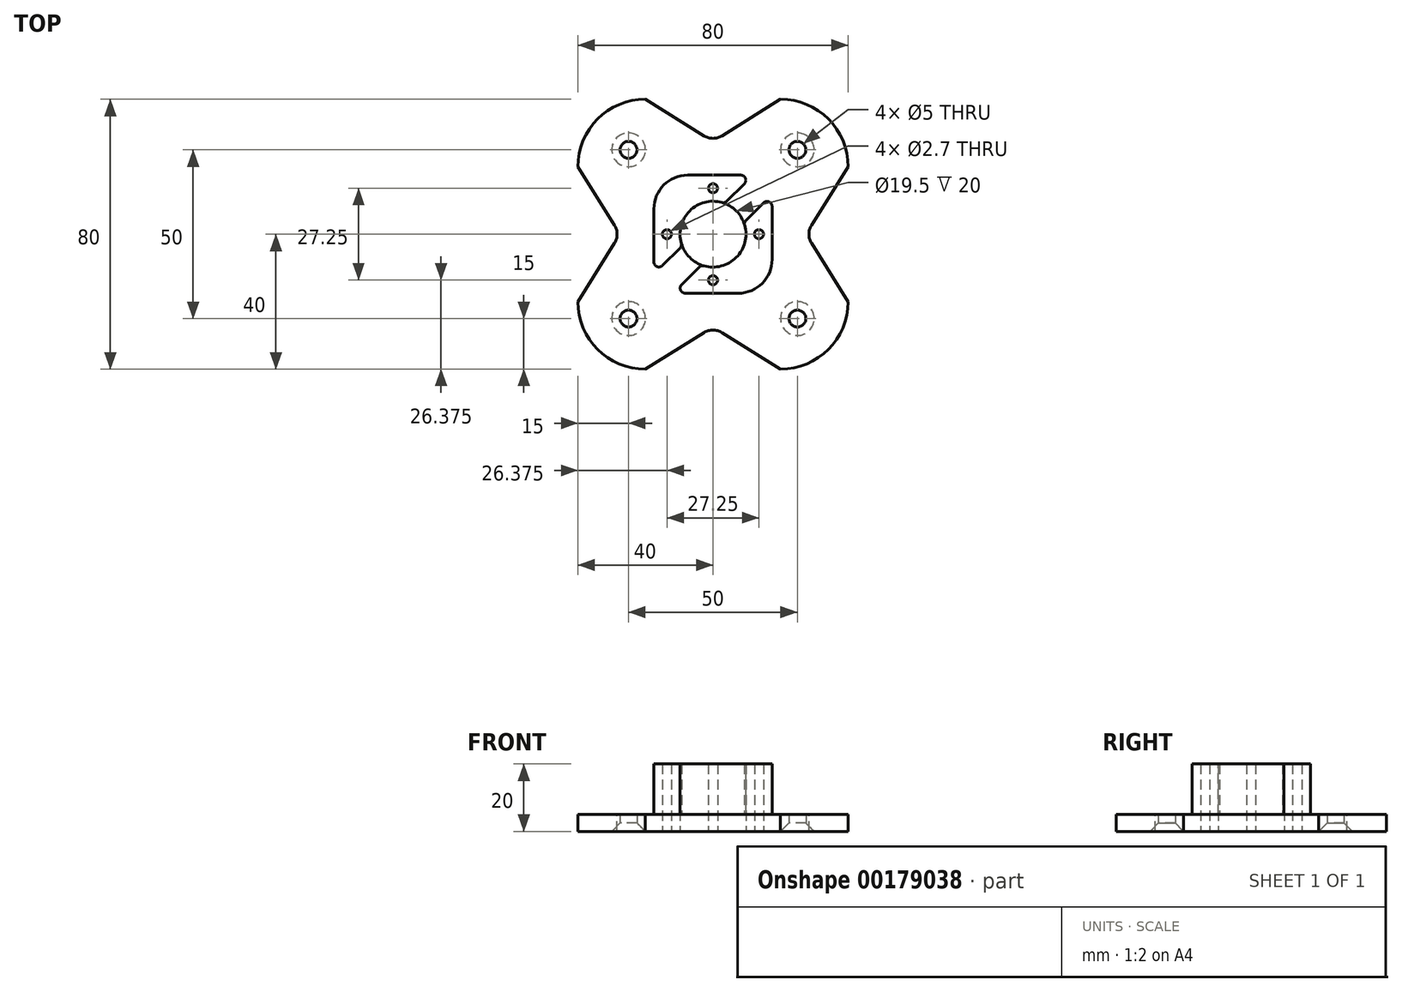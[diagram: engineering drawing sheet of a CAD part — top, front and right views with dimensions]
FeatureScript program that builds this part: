
annotation { "Feature Type Name" : "Feature", "Feature Type Description" : "" }
export const myFeature = defineFeature(function(context is Context, id is Id, definition is map)
    precondition{}
    {
        {
            var Q0;
            Q0=qCreatedBy(makeId("Top.planeOp"),FACE);
            var sketch = newSketch(context, id + "F0", { "sketchPlane" : qUnion([Q0])});
            skCircle(sketch, "E0", {"center": v(0, 0) * mm, "radius": 9.75 * mm});
            skLineSegment(sketch, "E1.bottom", {"start": v(-40, 40) * mm, "end": v(40, 40) * mm});
            skLineSegment(sketch, "E1.top", {"start": v(-40, -40) * mm, "end": v(40, -40) * mm});
            skLineSegment(sketch, "E1.left", {"start": v(-40, 40) * mm, "end": v(-40, -40) * mm});
            skLineSegment(sketch, "E1.right", {"start": v(40, 40) * mm, "end": v(40, -40) * mm});
            skCircle(sketch, "E2", {"center": v(-25, 25) * mm, "radius": 2.5 * mm});
            skCircle(sketch, "E3.0.1.0", {"center": v(-25, -25) * mm, "radius": 2.5 * mm});
            skCircle(sketch, "E3.1.0.0", {"center": v(25, 25) * mm, "radius": 2.5 * mm});
            skCircle(sketch, "E3.1.1.0", {"center": v(25, -25) * mm, "radius": 2.5 * mm});
            skLineSegment(sketch, "E3.direction1", {"start": v(-25, 25) * mm, "end": v(25, 25) * mm, "construction": true});
            skLineSegment(sketch, "E3.direction2", {"start": v(-25, 25) * mm, "end": v(-25, -25) * mm, "construction": true});
            skSolve(sketch);
        }
        {
            var Q0;
            Q0 = qSketchRegion(id + "F0", true);
            extrude(context, id + "F1", {"entities" : qUnion([Q0]), "depth" : 5 * mm});
        }
        {
            var Q0;
            Q0=makeQuery(id+"F1.opExtrude","CAP_EDGE",EDGE,{"disambiguationData":[OSD([sQuery(id+"F0.wireOp",EDGE,"E3.1.0.0")])],"isStart":true});
            var Q1;
            Q1=makeQuery(id+"F1.opExtrude","CAP_EDGE",EDGE,{"disambiguationData":[OSD([sQuery(id+"F0.wireOp",EDGE,"E2")])],"isStart":true});
            var Q2;
            Q2=makeQuery(id+"F1.opExtrude","CAP_EDGE",EDGE,{"disambiguationData":[OSD([sQuery(id+"F0.wireOp",EDGE,"E3.0.1.0")])],"isStart":true});
            var Q3;
            Q3=makeQuery(id+"F1.opExtrude","CAP_EDGE",EDGE,{"disambiguationData":[OSD([sQuery(id+"F0.wireOp",EDGE,"E3.1.1.0")])],"isStart":true});
            chamfer(context, id + "F2", {"entities" : qUnion([Q0, Q1, Q2, Q3]), "width" : 2.5 * mm, "tangentPropagation" : true});
        }
        {
            var Q0;
            Q0=makeQuery(id+"F1.opExtrude","CAP_FACE",FACE,{"disambiguationData":[OSD([sQuery(id+"F0.wireOp",EDGE,"E0"),sQuery(id+"F0.wireOp",EDGE,"E1.bottom"),sQuery(id+"F0.wireOp",EDGE,"E1.top"),sQuery(id+"F0.wireOp",EDGE,"E1.left"),sQuery(id+"F0.wireOp",EDGE,"E1.right"),sQuery(id+"F0.wireOp",EDGE,"E2"),sQuery(id+"F0.wireOp",EDGE,"E3.0.1.0"),sQuery(id+"F0.wireOp",EDGE,"E3.1.0.0"),sQuery(id+"F0.wireOp",EDGE,"E3.1.1.0")])],"isStart":false});
            var sketch = newSketch(context, id + "F3", { "sketchPlane" : qUnion([Q0])});
            skArc(sketch, "E4.0", {"start": v(-3.46, -9.12) * mm, "mid": v(6.9, -6.9) * mm, "end": v(9.12, 3.46) * mm});
            skLineSegment(sketch, "E5", {"start": v(-13.05, -7.4) * mm, "end": v(-9.12, -3.46) * mm});
            skLineSegment(sketch, "E6", {"start": v(-7.4, -13.05) * mm, "end": v(-3.46, -9.12) * mm});
            skArc(sketch, "E7.trimOffspring", {"start": v(3.46, 9.12) * mm, "mid": v(-6.9, 6.9) * mm, "end": v(-9.12, -3.46) * mm});
            skLineSegment(sketch, "E8.trimOffspring", {"start": v(3.46, 9.12) * mm, "end": v(7.4, 13.05) * mm});
            skLineSegment(sketch, "E9.trimOffspring", {"start": v(9.12, 3.46) * mm, "end": v(13.05, 7.4) * mm});
            skLineSegment(sketch, "E10", {"start": v(0, 0) * mm, "end": v(17.61, 17.61) * mm, "construction": true});
            skLineSegment(sketch, "E11.bottom", {"start": v(-17.5, 17.5) * mm, "end": v(17.5, 17.5) * mm});
            skLineSegment(sketch, "E11.top", {"start": v(-17.5, -17.5) * mm, "end": v(17.5, -17.5) * mm});
            skLineSegment(sketch, "E11.left", {"start": v(-17.5, 17.5) * mm, "end": v(-17.5, -17.5) * mm});
            skLineSegment(sketch, "E11.right", {"start": v(17.5, 17.5) * mm, "end": v(17.5, -17.5) * mm});
            skLineSegment(sketch, "E12", {"start": v(7.4, 13.05) * mm, "end": v(11.84, 17.5) * mm});
            skLineSegment(sketch, "E13", {"start": v(13.05, 7.4) * mm, "end": v(17.5, 11.84) * mm});
            skLineSegment(sketch, "E14", {"start": v(-13.05, -7.4) * mm, "end": v(-17.5, -11.84) * mm});
            skLineSegment(sketch, "E15", {"start": v(-7.4, -13.05) * mm, "end": v(-11.84, -17.5) * mm});
            skCircle(sketch, "E16", {"center": v(0, 13.63) * mm, "radius": 1.35 * mm});
            skCircle(sketch, "E17.1.0", {"center": v(-13.63, 0) * mm, "radius": 1.35 * mm});
            skCircle(sketch, "E17.2.0", {"center": v(0, -13.63) * mm, "radius": 1.35 * mm});
            skCircle(sketch, "E17.3.0", {"center": v(13.63, 0) * mm, "radius": 1.35 * mm});
            skLineSegment(sketch, "E18", {"start": v(0, 9.75) * mm, "end": v(0, 17.5) * mm, "construction": true});
            skSolve(sketch);
        }
        {
            var Q0;
            Q0=makeQuery(id+"F3.imprint","IMPRINT",FACE,{"disambiguationData":[TD([[makeQuery(id+"F3.imprint","IMPRINT",EDGE,{"derivedFrom":sQuery(id+"F3.wireOp",EDGE,"E4.0")}),-1.0]])]});
            var Q1;
            Q1=makeQuery(id+"F3.imprint","IMPRINT",FACE,{"disambiguationData":[TD([[makeQuery(id+"F3.imprint","IMPRINT",EDGE,{"derivedFrom":sQuery(id+"F3.wireOp",EDGE,"E5")}),1.0]])]});
            extrude(context, id + "F4", {"entities" : qUnion([Q0, Q1]), "operationType" : NewBodyOperationType.ADD, "depth" : 15 * mm});
        }
        {
            var Q0;
            Q0=makeQuery(id+"F4.boolean.opBoolean","SPLIT",FACE,{"disambiguationData":[TD([makeQuery(id+"F4.opExtrude","SWEPT_FACE",FACE,{"disambiguationData":[OSD([sQuery(id+"F3.wireOp",EDGE,"E17.1.0")])]})])],"derivedFrom":makeQuery(id+"F1.opExtrude","CAP_FACE",FACE,{"disambiguationData":[OSD([sQuery(id+"F0.wireOp",EDGE,"E0"),sQuery(id+"F0.wireOp",EDGE,"E1.bottom"),sQuery(id+"F0.wireOp",EDGE,"E1.top"),sQuery(id+"F0.wireOp",EDGE,"E1.left"),sQuery(id+"F0.wireOp",EDGE,"E1.right"),sQuery(id+"F0.wireOp",EDGE,"E2"),sQuery(id+"F0.wireOp",EDGE,"E3.0.1.0"),sQuery(id+"F0.wireOp",EDGE,"E3.1.0.0"),sQuery(id+"F0.wireOp",EDGE,"E3.1.1.0")])],"isStart":false})});
            var Q1;
            Q1=makeQuery(id+"F4.boolean.opBoolean","SPLIT",FACE,{"disambiguationData":[TD([makeQuery(id+"F4.opExtrude","SWEPT_FACE",FACE,{"disambiguationData":[OSD([sQuery(id+"F3.wireOp",EDGE,"E16")])]})])],"derivedFrom":makeQuery(id+"F1.opExtrude","CAP_FACE",FACE,{"disambiguationData":[OSD([sQuery(id+"F0.wireOp",EDGE,"E0"),sQuery(id+"F0.wireOp",EDGE,"E1.bottom"),sQuery(id+"F0.wireOp",EDGE,"E1.top"),sQuery(id+"F0.wireOp",EDGE,"E1.left"),sQuery(id+"F0.wireOp",EDGE,"E1.right"),sQuery(id+"F0.wireOp",EDGE,"E2"),sQuery(id+"F0.wireOp",EDGE,"E3.0.1.0"),sQuery(id+"F0.wireOp",EDGE,"E3.1.0.0"),sQuery(id+"F0.wireOp",EDGE,"E3.1.1.0")])],"isStart":false})});
            var Q2;
            Q2=makeQuery(id+"F4.boolean.opBoolean","SPLIT",FACE,{"disambiguationData":[TD([makeQuery(id+"F4.opExtrude","SWEPT_FACE",FACE,{"disambiguationData":[OSD([sQuery(id+"F3.wireOp",EDGE,"E17.3.0")])]})])],"derivedFrom":makeQuery(id+"F1.opExtrude","CAP_FACE",FACE,{"disambiguationData":[OSD([sQuery(id+"F0.wireOp",EDGE,"E0"),sQuery(id+"F0.wireOp",EDGE,"E1.bottom"),sQuery(id+"F0.wireOp",EDGE,"E1.top"),sQuery(id+"F0.wireOp",EDGE,"E1.left"),sQuery(id+"F0.wireOp",EDGE,"E1.right"),sQuery(id+"F0.wireOp",EDGE,"E2"),sQuery(id+"F0.wireOp",EDGE,"E3.0.1.0"),sQuery(id+"F0.wireOp",EDGE,"E3.1.0.0"),sQuery(id+"F0.wireOp",EDGE,"E3.1.1.0")])],"isStart":false})});
            var Q3;
            Q3=makeQuery(id+"F4.boolean.opBoolean","SPLIT",FACE,{"disambiguationData":[TD([makeQuery(id+"F4.opExtrude","SWEPT_FACE",FACE,{"disambiguationData":[OSD([sQuery(id+"F3.wireOp",EDGE,"E17.2.0")])]})])],"derivedFrom":makeQuery(id+"F1.opExtrude","CAP_FACE",FACE,{"disambiguationData":[OSD([sQuery(id+"F0.wireOp",EDGE,"E0"),sQuery(id+"F0.wireOp",EDGE,"E1.bottom"),sQuery(id+"F0.wireOp",EDGE,"E1.top"),sQuery(id+"F0.wireOp",EDGE,"E1.left"),sQuery(id+"F0.wireOp",EDGE,"E1.right"),sQuery(id+"F0.wireOp",EDGE,"E2"),sQuery(id+"F0.wireOp",EDGE,"E3.0.1.0"),sQuery(id+"F0.wireOp",EDGE,"E3.1.0.0"),sQuery(id+"F0.wireOp",EDGE,"E3.1.1.0")])],"isStart":false})});
            extrude(context, id + "F5", {"entities" : qUnion([Q0, Q1, Q2, Q3]), "operationType" : NewBodyOperationType.REMOVE, "endBound" : BoundingType.THROUGH_ALL, "oppositeDirection" : true, "depth" : 25 * mm});
        }
        {
            var Q0;
            Q0=makeQuery(id+"F1.opExtrude","SWEPT_EDGE",EDGE,{"disambiguationData":[OSD([sQuery(id+"F0.wireOp",EDGE,"E1.bottom"),sQuery(id+"F0.wireOp",EDGE,"E1.left")])]});
            var Q1;
            Q1=makeQuery(id+"F1.opExtrude","SWEPT_EDGE",EDGE,{"disambiguationData":[OSD([sQuery(id+"F0.wireOp",EDGE,"E1.bottom"),sQuery(id+"F0.wireOp",EDGE,"E1.right")])]});
            var Q2;
            Q2=makeQuery(id+"F1.opExtrude","SWEPT_EDGE",EDGE,{"disambiguationData":[OSD([sQuery(id+"F0.wireOp",EDGE,"E1.top"),sQuery(id+"F0.wireOp",EDGE,"E1.right")])]});
            var Q3;
            Q3=makeQuery(id+"F1.opExtrude","SWEPT_EDGE",EDGE,{"disambiguationData":[OSD([sQuery(id+"F0.wireOp",EDGE,"E1.top"),sQuery(id+"F0.wireOp",EDGE,"E1.left")])]});
            fillet(context, id + "F6", {"entities" : qUnion([Q0, Q1, Q2, Q3]), "radius" : 20 * mm, "tangentPropagation" : true, "allowEdgeOverflow" : false});
        }
        {
            var Q0;
            Q0=makeQuery(id+"F4.opExtrude","SWEPT_EDGE",EDGE,{"disambiguationData":[OSD([sQuery(id+"F3.wireOp",EDGE,"E11.bottom"),sQuery(id+"F3.wireOp",EDGE,"E11.left")])]});
            var Q1;
            Q1=makeQuery(id+"F4.opExtrude","SWEPT_EDGE",EDGE,{"disambiguationData":[OSD([sQuery(id+"F3.wireOp",EDGE,"E11.top"),sQuery(id+"F3.wireOp",EDGE,"E11.right")])]});
            fillet(context, id + "F7", {"entities" : qUnion([Q0, Q1]), "radius" : 10 * mm, "tangentPropagation" : true, "allowEdgeOverflow" : false});
        }
        {
            var Q0;
            {var subQ0=sQuery(id+"F0.wireOp",EDGE,"E3.1.1.0");var subQ1=sQuery(id+"F0.wireOp",EDGE,"E3.1.0.0");var subQ2=sQuery(id+"F0.wireOp",EDGE,"E3.0.1.0");var subQ3=sQuery(id+"F0.wireOp",EDGE,"E2");var subQ4=sQuery(id+"F0.wireOp",EDGE,"E1.right");var subQ5=sQuery(id+"F0.wireOp",EDGE,"E0");var subQ6=sQuery(id+"F0.wireOp",EDGE,"E1.left");var subQ7=sQuery(id+"F0.wireOp",EDGE,"E1.bottom");var subQ8=sQuery(id+"F0.wireOp",EDGE,"E1.top");Q0=makeQuery(id+"F4.boolean.opBoolean","SPLIT",FACE,{"disambiguationData":[TD([makeQuery(id+"F1.opExtrude","SWEPT_FACE",FACE,{"disambiguationData":[OSD([subQ5])]})])],"derivedFrom":makeQuery(id+"F1.opExtrude","CAP_FACE",FACE,{"disambiguationData":[OSD([subQ5,subQ7,subQ8,subQ6,subQ4,subQ3,subQ2,subQ1,subQ0])],"isStart":false})});}
            var sketch = newSketch(context, id + "F8", { "sketchPlane" : qUnion([Q0])});
            skLineSegment(sketch, "E19", {"start": v(-2.65, 29.16) * mm, "end": v(-20, 40) * mm});
            skLineSegment(sketch, "E20", {"start": v(-20, 40) * mm, "end": v(20, 40) * mm});
            skLineSegment(sketch, "E21", {"start": v(20, 40) * mm, "end": v(2.65, 29.16) * mm});
            skPoint(sketch, "E22.visualSharp", {"position": v(0, 27.5) * mm});
            skArc(sketch, "E22.filletArc", {"start": v(-2.65, 29.16) * mm, "mid": v(0, 28.4) * mm, "end": v(2.65, 29.16) * mm});
            skLineSegment(sketch, "E23.1.0", {"start": v(-40, -20) * mm, "end": v(-40, 20) * mm});
            skLineSegment(sketch, "E23.1.1", {"start": v(-29.16, -2.65) * mm, "end": v(-40, -20) * mm});
            skArc(sketch, "E23.1.2", {"start": v(-29.16, -2.65) * mm, "mid": v(-28.4, 0) * mm, "end": v(-29.16, 2.65) * mm});
            skLineSegment(sketch, "E23.1.3", {"start": v(-40, 20) * mm, "end": v(-29.16, 2.65) * mm});
            skLineSegment(sketch, "E23.2.0", {"start": v(20, -40) * mm, "end": v(-20, -40) * mm});
            skLineSegment(sketch, "E23.2.1", {"start": v(2.65, -29.16) * mm, "end": v(20, -40) * mm});
            skArc(sketch, "E23.2.2", {"start": v(2.65, -29.16) * mm, "mid": v(0, -28.4) * mm, "end": v(-2.65, -29.16) * mm});
            skLineSegment(sketch, "E23.2.3", {"start": v(-20, -40) * mm, "end": v(-2.65, -29.16) * mm});
            skLineSegment(sketch, "E23.3.0", {"start": v(40, 20) * mm, "end": v(40, -20) * mm});
            skLineSegment(sketch, "E23.3.1", {"start": v(29.16, 2.65) * mm, "end": v(40, 20) * mm});
            skArc(sketch, "E23.3.2", {"start": v(29.16, 2.65) * mm, "mid": v(28.4, 0) * mm, "end": v(29.16, -2.65) * mm});
            skLineSegment(sketch, "E23.3.3", {"start": v(40, -20) * mm, "end": v(29.16, -2.65) * mm});
            skPoint(sketch, "E23.center", {"position": v(0, 0) * mm});
            skSolve(sketch);
        }
        {
            var Q0;
            Q0 = qSketchRegion(id + "F8", true);
            extrude(context, id + "F9", {"entities" : qUnion([Q0]), "operationType" : NewBodyOperationType.REMOVE, "endBound" : BoundingType.THROUGH_ALL, "oppositeDirection" : true, "depth" : 25 * mm});
        }
        {
            var Q0;
            Q0=makeQuery(id+"F4.opExtrude","SWEPT_EDGE",EDGE,{"disambiguationData":[OSD([sQuery(id+"F0.wireOp",EDGE,"E0"),sQuery(id+"F3.wireOp",EDGE,"E5"),sQuery(id+"F3.wireOp",EDGE,"E7.trimOffspring")])]});
            var Q1;
            Q1=makeQuery(id+"F4.opExtrude","SWEPT_EDGE",EDGE,{"disambiguationData":[OSD([sQuery(id+"F3.wireOp",EDGE,"E11.left"),sQuery(id+"F3.wireOp",EDGE,"E14")])]});
            var Q2;
            Q2=makeQuery(id+"F4.opExtrude","SWEPT_EDGE",EDGE,{"disambiguationData":[OSD([sQuery(id+"F3.wireOp",EDGE,"E11.top"),sQuery(id+"F3.wireOp",EDGE,"E15")])]});
            var Q3;
            Q3=makeQuery(id+"F4.opExtrude","SWEPT_EDGE",EDGE,{"disambiguationData":[OSD([sQuery(id+"F0.wireOp",EDGE,"E0"),sQuery(id+"F3.wireOp",EDGE,"E4.0"),sQuery(id+"F3.wireOp",EDGE,"E6")])]});
            var Q4;
            Q4=makeQuery(id+"F4.opExtrude","SWEPT_EDGE",EDGE,{"disambiguationData":[OSD([sQuery(id+"F0.wireOp",EDGE,"E0"),sQuery(id+"F3.wireOp",EDGE,"E4.0"),sQuery(id+"F3.wireOp",EDGE,"E9.trimOffspring")])]});
            var Q5;
            Q5=makeQuery(id+"F4.opExtrude","SWEPT_EDGE",EDGE,{"disambiguationData":[OSD([sQuery(id+"F3.wireOp",EDGE,"E11.right"),sQuery(id+"F3.wireOp",EDGE,"E13")])]});
            var Q6;
            Q6=makeQuery(id+"F4.opExtrude","SWEPT_EDGE",EDGE,{"disambiguationData":[OSD([sQuery(id+"F0.wireOp",EDGE,"E0"),sQuery(id+"F3.wireOp",EDGE,"E7.trimOffspring"),sQuery(id+"F3.wireOp",EDGE,"E8.trimOffspring")])]});
            var Q7;
            Q7=makeQuery(id+"F4.opExtrude","SWEPT_EDGE",EDGE,{"disambiguationData":[OSD([sQuery(id+"F3.wireOp",EDGE,"E11.bottom"),sQuery(id+"F3.wireOp",EDGE,"E12")])]});
            fillet(context, id + "F10", {"entities" : qUnion([Q0, Q1, Q2, Q3, Q4, Q5, Q6, Q7]), "radius" : 1.5 * mm, "tangentPropagation" : true, "allowEdgeOverflow" : false});
        }
    });
